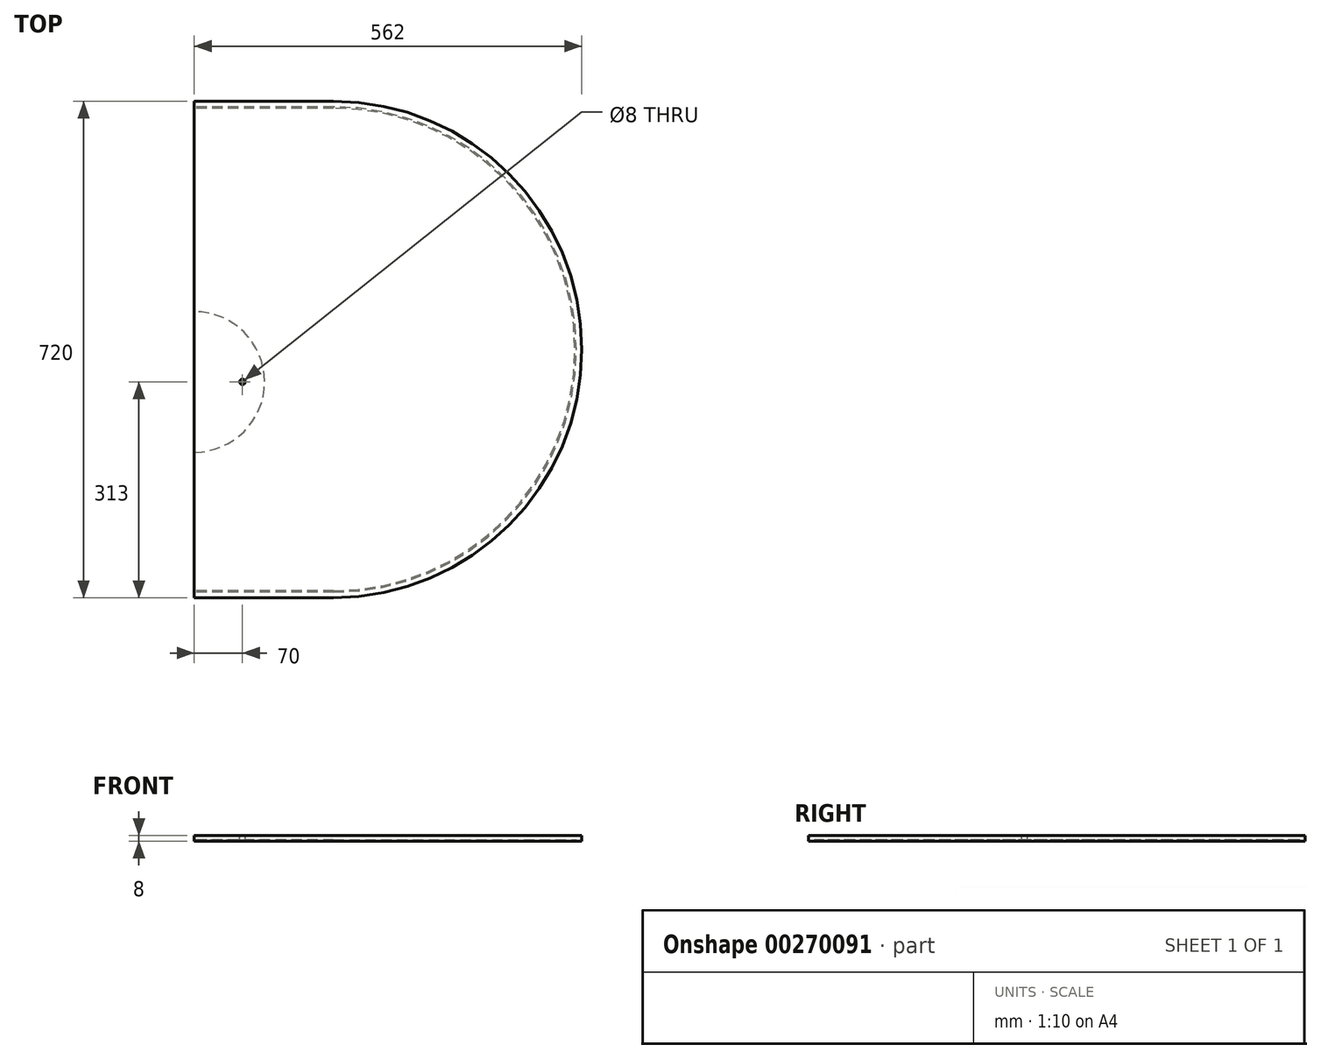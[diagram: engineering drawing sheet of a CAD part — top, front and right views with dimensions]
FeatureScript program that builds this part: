
annotation { "Feature Type Name" : "Feature", "Feature Type Description" : "" }
export const myFeature = defineFeature(function(context is Context, id is Id, definition is map)
    precondition{}
    {
        {
            var Q0;
            Q0=qCreatedBy(makeId("Top.planeOp"),FACE);
            var sketch = newSketch(context, id + "F0", { "sketchPlane" : qUnion([Q0])});
            skArc(sketch, "E0", {"start": v(0, -360) * mm, "mid": v(360, 0) * mm, "end": v(0, 360) * mm});
            skLineSegment(sketch, "E1.bottom", {"start": v(0, 360) * mm, "end": v(-202, 360) * mm});
            skLineSegment(sketch, "E1.top", {"start": v(0, -360) * mm, "end": v(-202, -360) * mm});
            skLineSegment(sketch, "E1.right", {"start": v(-202, 360) * mm, "end": v(-202, -360) * mm});
            skSolve(sketch);
        }
        {
            var Q0;
            Q0=makeQuery(id+"F0.imprint","IMPRINT",FACE,{"disambiguationData":[TD([[makeQuery(id+"F0.imprint","IMPRINT",EDGE,{"derivedFrom":sQuery(id+"F0.wireOp",EDGE,"E0")}),1.0]])]});
            extrude(context, id + "F1", {"entities" : qUnion([Q0]), "depth" : 8 * mm});
        }
        {
            var Q0;
            Q0=makeQuery(id+"F1.opExtrude","CAP_FACE",FACE,{"disambiguationData":[OSD([sQuery(id+"F0.wireOp",EDGE,"E0"),sQuery(id+"F0.wireOp",EDGE,"E1.bottom"),sQuery(id+"F0.wireOp",EDGE,"E1.top"),sQuery(id+"F0.wireOp",EDGE,"E1.right")])],"isStart":true});
            var sketch = newSketch(context, id + "F2", { "sketchPlane" : qUnion([Q0])});
            skArc(sketch, "E2", {"start": v(0, -350) * mm, "mid": v(350, 0) * mm, "end": v(0, 350) * mm});
            skArc(sketch, "E3.0", {"start": v(0, -352) * mm, "mid": v(352, 0) * mm, "end": v(0, 352) * mm});
            skLineSegment(sketch, "E4", {"start": v(0, -350) * mm, "end": v(0, 350) * mm});
            skPoint(sketch, "E5.orphan", {"position": v(0, -431.73) * mm});
            skLineSegment(sketch, "E6", {"start": v(0, -352) * mm, "end": v(-202, -352) * mm});
            skLineSegment(sketch, "E7", {"start": v(0, -350) * mm, "end": v(-202, -350) * mm});
            skLineSegment(sketch, "E8", {"start": v(0, 350) * mm, "end": v(-202, 350) * mm});
            skLineSegment(sketch, "E9", {"start": v(0, 352) * mm, "end": v(-202, 352) * mm});
            skSolve(sketch);
        }
        {
            var Q0;
            Q0=makeQuery(id+"F2.imprint","IMPRINT",FACE,{"disambiguationData":[TD([[makeQuery(id+"F2.imprint","IMPRINT",EDGE,{"derivedFrom":sQuery(id+"F2.wireOp",EDGE,"E2")}),-1.0]])]});
            extrude(context, id + "F3", {"entities" : qUnion([Q0]), "operationType" : NewBodyOperationType.REMOVE, "oppositeDirection" : true, "depth" : 2 * mm});
        }
        {
            var Q0;
            Q0=makeQuery(id+"F1.opExtrude","CAP_FACE",FACE,{"disambiguationData":[OSD([sQuery(id+"F0.wireOp",EDGE,"E0"),sQuery(id+"F0.wireOp",EDGE,"E1.bottom"),sQuery(id+"F0.wireOp",EDGE,"E1.top"),sQuery(id+"F0.wireOp",EDGE,"E1.right")])],"isStart":false});
            var sketch = newSketch(context, id + "F4", { "sketchPlane" : qUnion([Q0])});
            skCircle(sketch, "E10", {"center": v(-132, -47) * mm, "radius": 4 * mm});
            skLineSegment(sketch, "E11", {"start": v(-137.26, -149) * mm, "end": v(-830.48, -149) * mm, "construction": true});
            skArc(sketch, "E12", {"start": v(-202, -149) * mm, "mid": v(-100, -47) * mm, "end": v(-202, 55) * mm});
            skSolve(sketch);
        }
        {
            var Q0;
            Q0=makeQuery(id+"F4.imprint","IMPRINT",FACE,{"disambiguationData":[TD([[makeQuery(id+"F4.imprint","IMPRINT",EDGE,{"derivedFrom":sQuery(id+"F4.wireOp",EDGE,"E10")}),1.0]])]});
            extrude(context, id + "F5", {"entities" : qUnion([Q0]), "operationType" : NewBodyOperationType.REMOVE, "endBound" : BoundingType.UP_TO_NEXT, "oppositeDirection" : true, "depth" : 25 * mm});
        }
        {
            var Q0;
            Q0=makeQuery(id+"F2.imprint","IMPRINT",FACE,{"disambiguationData":[TD([[makeQuery(id+"F2.imprint","IMPRINT",EDGE,{"derivedFrom":sQuery(id+"F2.wireOp",EDGE,"E4")}),1.0]])]});
            var sketch = newSketch(context, id + "F6", { "sketchPlane" : qUnion([Q0])});
            skLineSegment(sketch, "E13", {"start": v(-541.54, 149) * mm, "end": v(32.37, 149) * mm, "construction": true});
            skArc(sketch, "E14", {"start": v(-202, -55) * mm, "mid": v(-100, 47) * mm, "end": v(-202, 149) * mm});
            skLineSegment(sketch, "E15", {"start": v(-202, 149) * mm, "end": v(-202, -55) * mm});
            skSolve(sketch);
        }
        {
            var Q0;
            Q0=makeQuery(id+"F6.imprint","IMPRINT",FACE,{"disambiguationData":[TD([[makeQuery(id+"F6.imprint","IMPRINT",EDGE,{"derivedFrom":sQuery(id+"F6.wireOp",EDGE,"E14")}),1.0]])]});
            extrude(context, id + "F7", {"entities" : qUnion([Q0]), "operationType" : NewBodyOperationType.REMOVE, "oppositeDirection" : true, "depth" : 2 * mm});
        }
    });
